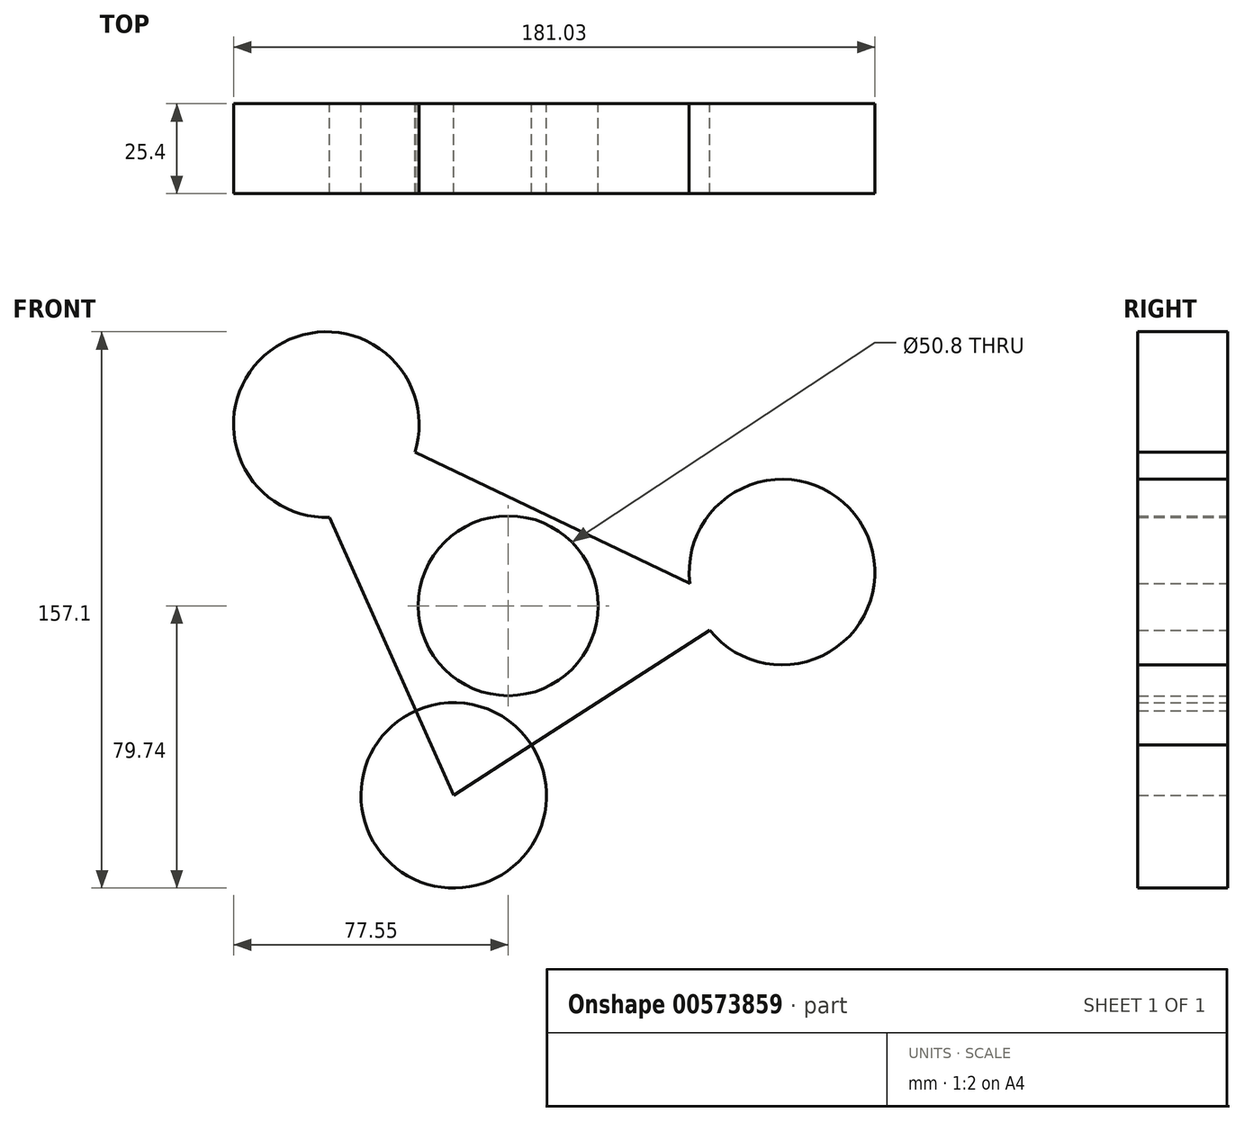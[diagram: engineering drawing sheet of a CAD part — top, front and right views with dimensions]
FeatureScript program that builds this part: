
annotation { "Feature Type Name" : "Feature", "Feature Type Description" : "" }
export const myFeature = defineFeature(function(context is Context, id is Id, definition is map)
    precondition{}
    {
        {
            var Q0;
            Q0=qCreatedBy(makeId("Front.planeOp"),FACE);
            var sketch = newSketch(context, id + "F0", { "sketchPlane" : qUnion([Q0])});
            skCircle(sketch, "E0", {"center": v(-51.34, 51.16) * mm, "radius": 26.2 * mm});
            skCircle(sketch, "E1", {"center": v(77.27, 9.5) * mm, "radius": 26.2 * mm});
            skLineSegment(sketch, "E2", {"start": v(-26.34, 43.33) * mm, "end": v(51.27, 6.3) * mm});
            skLineSegment(sketch, "E3", {"start": v(56.86, -6.94) * mm, "end": v(-15.4, -53.56) * mm});
            skCircle(sketch, "E4", {"center": v(-15.4, -53.56) * mm, "radius": 26.18 * mm});
            skLineSegment(sketch, "E5", {"start": v(-50.43, 24.97) * mm, "end": v(-15.4, -53.56) * mm});
            skSolve(sketch);
        }
        {
            var Q0;
            {var subQ0=sQuery(id+"F0.wireOp",EDGE,"E0");var subQ1=makeQuery(id+"F0.imprint","INTERSECT",VERTEX,{"derivedFrom":[subQ0,sQuery(id+"F0.wireOp",EDGE,"E2")]});Q0=makeQuery(id+"F0.imprint","IMPRINT",FACE,{"disambiguationData":[TD([[makeQuery(id+"F0.imprint","IMPRINT",EDGE,{"disambiguationData":[TD([[subQ1,1.0]])],"derivedFrom":subQ0}),1.0]])]});}
            var Q1;
            {var subQ0=sQuery(id+"F0.wireOp",EDGE,"E5");var subQ1=sQuery(id+"F0.wireOp",EDGE,"E3");var subQ2=makeQuery(id+"F0.imprint","INTERSECT",VERTEX,{"derivedFrom":[subQ1,subQ0]});Q1=makeQuery(id+"F0.imprint","IMPRINT",FACE,{"disambiguationData":[TD([[makeQuery(id+"F0.imprint","IMPRINT",EDGE,{"disambiguationData":[TD([[subQ2,1.0]])],"derivedFrom":subQ1}),1.0]])]});}
            var Q2;
            {var subQ0=sQuery(id+"F0.wireOp",EDGE,"E1");var subQ1=makeQuery(id+"F0.imprint","INTERSECT",VERTEX,{"derivedFrom":[subQ0,sQuery(id+"F0.wireOp",EDGE,"E2")]});Q2=makeQuery(id+"F0.imprint","IMPRINT",FACE,{"disambiguationData":[TD([[makeQuery(id+"F0.imprint","IMPRINT",EDGE,{"disambiguationData":[TD([[subQ1,-1.0]])],"derivedFrom":subQ0}),1.0]])]});}
            var Q3;
            {var subQ0=sQuery(id+"F0.wireOp",EDGE,"E2");Q3=makeQuery(id+"F0.imprint","IMPRINT",FACE,{"disambiguationData":[TD([[makeQuery(id+"F0.imprint","IMPRINT",EDGE,{"derivedFrom":subQ0}),-1.0]])]});}
            extrude(context, id + "F1", {"entities" : qUnion([Q0, Q1, Q2, Q3]), "depth" : 25.4 * mm, "offsetDistance" : 25.4 * mm});
        }
        {
            var Q0;
            Q0=qCreatedBy(makeId("Front.planeOp"),FACE);
            var sketch = newSketch(context, id + "F2", { "sketchPlane" : qUnion([Q0])});
            skCircle(sketch, "E6", {"center": v(0, 0) * mm, "radius": 24.73 * mm});
            skSolve(sketch);
        }
        {
            var Q0;
            Q0=sQuery(id+"F2.wireOp",VERTEX,"E6.center");
            var Q1;
            Q1=makeQuery(id+"F1.opExtrude","SWEPT_BODY",BODY,{"disambiguationData":[OSD([sQuery(id+"F0.wireOp",EDGE,"E0"),sQuery(id+"F0.wireOp",EDGE,"E1"),sQuery(id+"F0.wireOp",EDGE,"E2"),sQuery(id+"F0.wireOp",EDGE,"E3"),sQuery(id+"F0.wireOp",EDGE,"E4"),sQuery(id+"F0.wireOp",EDGE,"E5")])]});
            hole(context, id + "F3", {"style" : HoleStyle.SIMPLE, "endStyle" : HoleEndStyle.THROUGH, "oppositeDirection" : true, "holeDiameter" : 50.8 * mm, "majorDiameter" : 6.35 * mm, "isTappedThrough" : true, "tappedDepth" : 12.7 * mm, "tapClearance" : 3, "locations" : qUnion([Q0]), "scope" : qUnion([Q1])});
        }
    });
